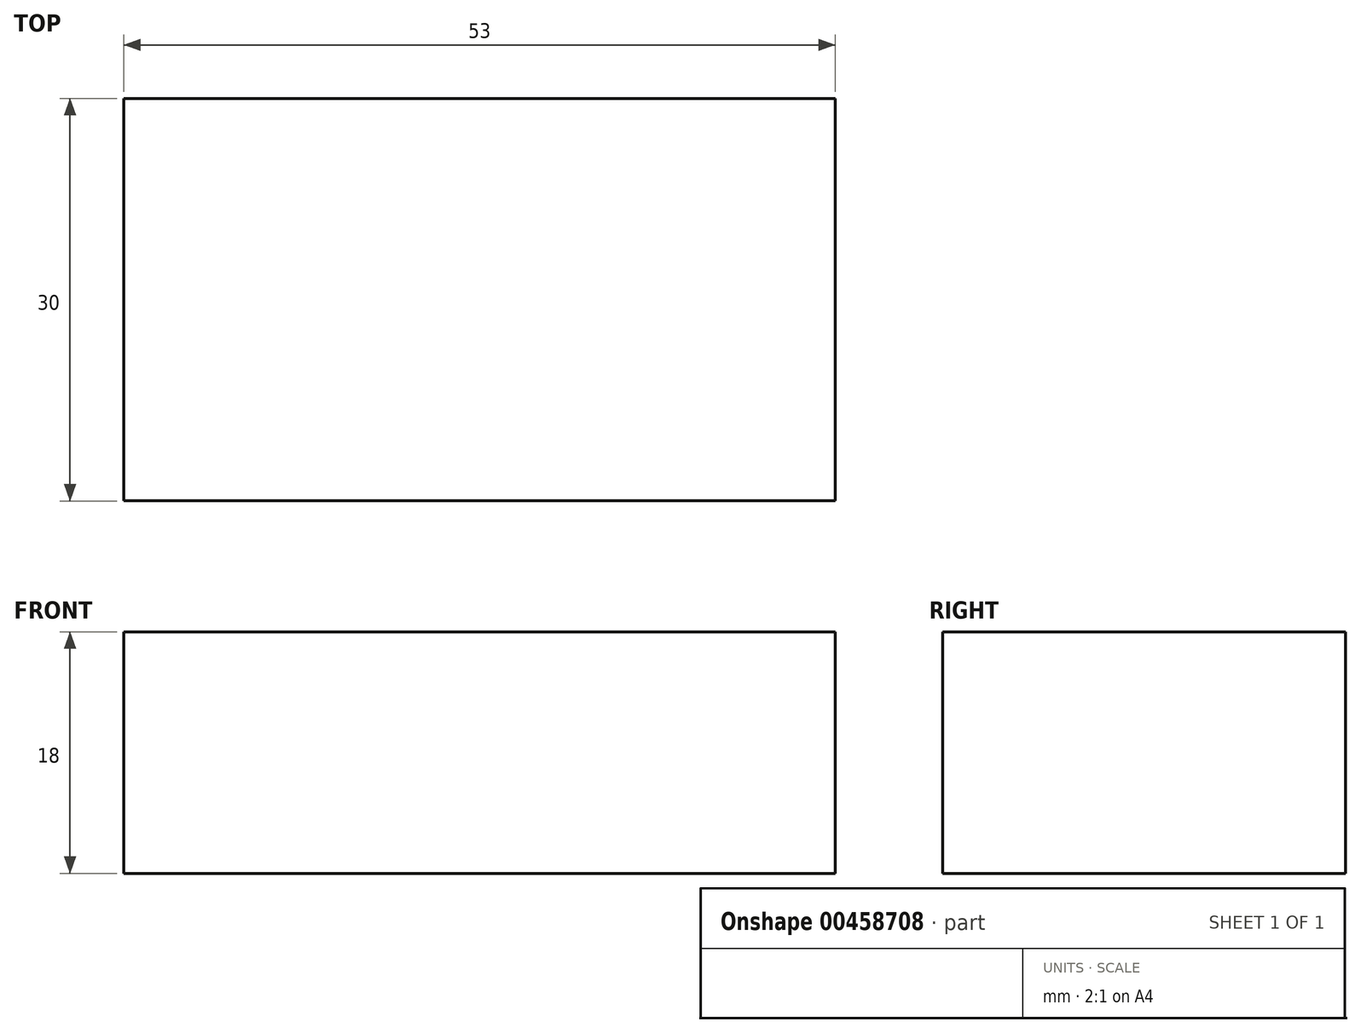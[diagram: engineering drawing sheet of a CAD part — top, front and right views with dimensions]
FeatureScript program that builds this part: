
annotation { "Feature Type Name" : "Feature", "Feature Type Description" : "" }
export const myFeature = defineFeature(function(context is Context, id is Id, definition is map)
    precondition{}
    {
        {
            var Q0;
            Q0=qCreatedBy(makeId("Top.planeOp"),FACE);
            var sketch = newSketch(context, id + "F0", { "sketchPlane" : qUnion([Q0])});
            skLineSegment(sketch, "E0.bottom", {"start": v(-23.42, 17.73) * mm, "end": v(29.58, 17.73) * mm});
            skLineSegment(sketch, "E0.top", {"start": v(-23.42, -12.27) * mm, "end": v(29.58, -12.27) * mm});
            skLineSegment(sketch, "E0.left", {"start": v(-23.42, 17.73) * mm, "end": v(-23.42, -12.27) * mm});
            skLineSegment(sketch, "E0.right", {"start": v(29.58, 17.73) * mm, "end": v(29.58, -12.27) * mm});
            skSolve(sketch);
        }
        {
            var Q0;
            Q0=makeQuery(id+"F0.imprint","IMPRINT",FACE,{"disambiguationData":[TD([[makeQuery(id+"F0.imprint","IMPRINT",EDGE,{"derivedFrom":sQuery(id+"F0.wireOp",EDGE,"E0.bottom")}),-1.0]])]});
            extrude(context, id + "F1", {"entities" : qUnion([Q0]), "depth" : 18 * mm, "offsetDistance" : 25 * mm, "symmetric" : true});
        }
    });
